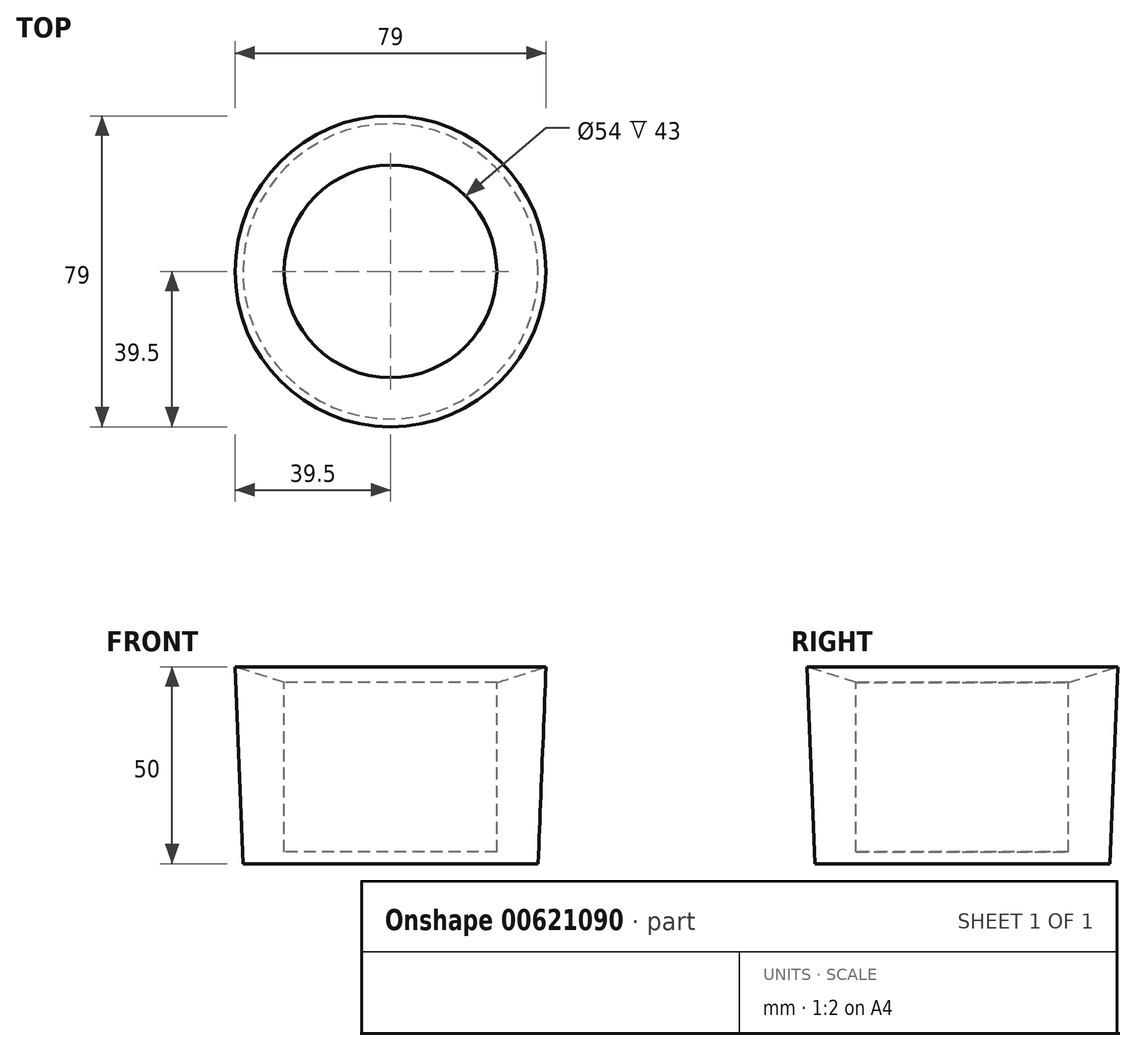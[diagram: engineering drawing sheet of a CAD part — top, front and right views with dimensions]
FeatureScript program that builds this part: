
annotation { "Feature Type Name" : "Feature", "Feature Type Description" : "" }
export const myFeature = defineFeature(function(context is Context, id is Id, definition is map)
    precondition{}
    {
        {
            var Q0;
            Q0=qCreatedBy(makeId("Right.planeOp"),FACE);
            var sketch = newSketch(context, id + "F0", { "sketchPlane" : qUnion([Q0])});
            skLineSegment(sketch, "E0", {"start": v(-39.5, 50) * mm, "end": v(-27, 46) * mm});
            skLineSegment(sketch, "E1", {"start": v(-27, 46) * mm, "end": v(-27, 3) * mm});
            skLineSegment(sketch, "E2", {"start": v(-27, 3) * mm, "end": v(0, 3) * mm});
            skLineSegment(sketch, "E3", {"start": v(0, 3) * mm, "end": v(0, 0) * mm});
            skLineSegment(sketch, "E4", {"start": v(0, 0) * mm, "end": v(-37.5, 0) * mm});
            skLineSegment(sketch, "E5", {"start": v(-37.5, 0) * mm, "end": v(-39.5, 50) * mm});
            skSolve(sketch);
        }
        {
            var Q0;
            Q0=makeQuery(id+"F0.imprint","IMPRINT",FACE,{"disambiguationData":[TD([[makeQuery(id+"F0.imprint","IMPRINT",EDGE,{"derivedFrom":sQuery(id+"F0.wireOp",EDGE,"E0")}),-1.0]])]});
            var Q1;
            Q1=sQuery(id+"F0.wireOp",EDGE,"E3");
            revolve(context, id + "F1", {"entities" : qUnion([Q0]), "axis" : qUnion([Q1]), "revolveType" : RevolveType.FULL});
        }
    });
